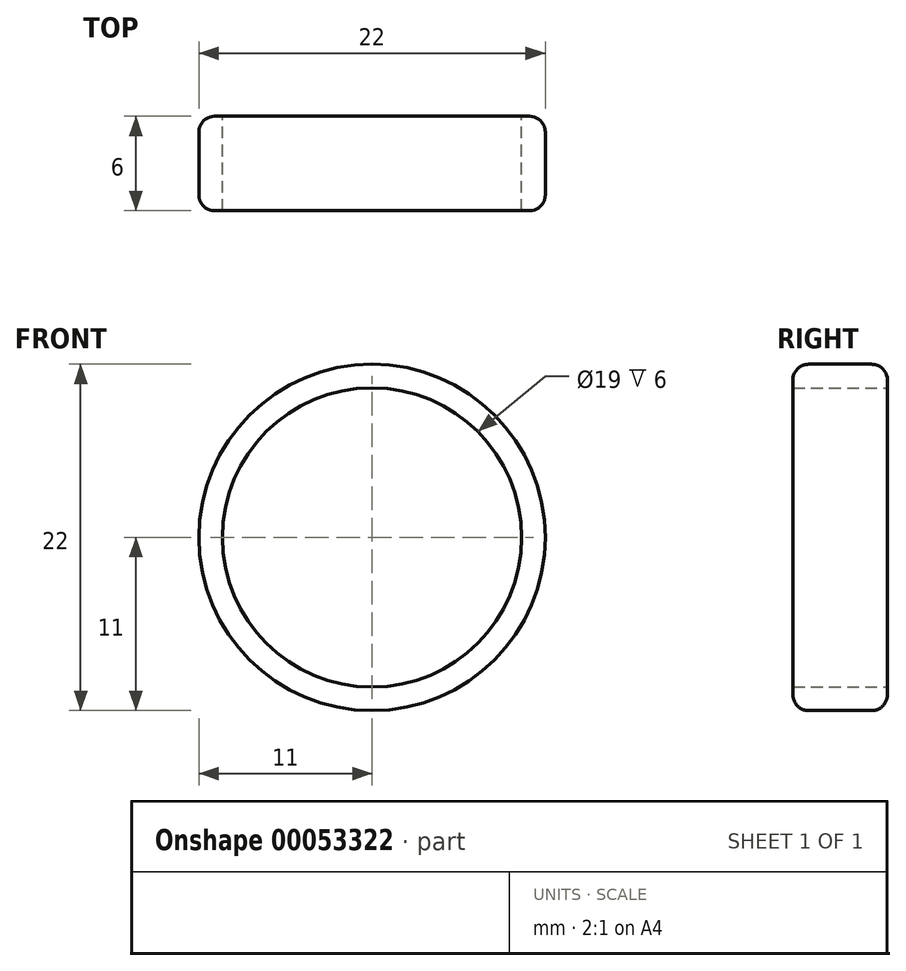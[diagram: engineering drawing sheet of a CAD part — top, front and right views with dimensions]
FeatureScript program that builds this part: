
annotation { "Feature Type Name" : "Feature", "Feature Type Description" : "" }
export const myFeature = defineFeature(function(context is Context, id is Id, definition is map)
    precondition{}
    {
        {
            var Q0;
            Q0=qCreatedBy(makeId("Front.planeOp"),FACE);
            var sketch = newSketch(context, id + "F0", { "sketchPlane" : qUnion([Q0])});
            skCircle(sketch, "E0", {"center": v(0, 0) * mm, "radius": 11 * mm});
            skCircle(sketch, "E1", {"center": v(0, 0) * mm, "radius": 9.5 * mm});
            skSolve(sketch);
        }
        {
            var Q0;
            Q0=makeQuery(id+"F0.imprint","IMPRINT",FACE,{"disambiguationData":[TD([[makeQuery(id+"F0.imprint","IMPRINT",EDGE,{"derivedFrom":sQuery(id+"F0.wireOp",EDGE,"E0")}),1.0]])]});
            extrude(context, id + "F1", {"entities" : qUnion([Q0]), "depth" : 6 * mm});
        }
        {
            var Q0;
            Q0=makeQuery(id+"F1.opExtrude","CAP_EDGE",EDGE,{"disambiguationData":[OSD([sQuery(id+"F0.wireOp",EDGE,"E0")])],"isStart":false});
            var Q1;
            Q1=makeQuery(id+"F1.opExtrude","CAP_EDGE",EDGE,{"disambiguationData":[OSD([sQuery(id+"F0.wireOp",EDGE,"E0")])],"isStart":true});
            fillet(context, id + "F2", {"entities" : qUnion([Q0, Q1]), "radius" : 1 * mm, "tangentPropagation" : true, "allowEdgeOverflow" : false});
        }
    });
